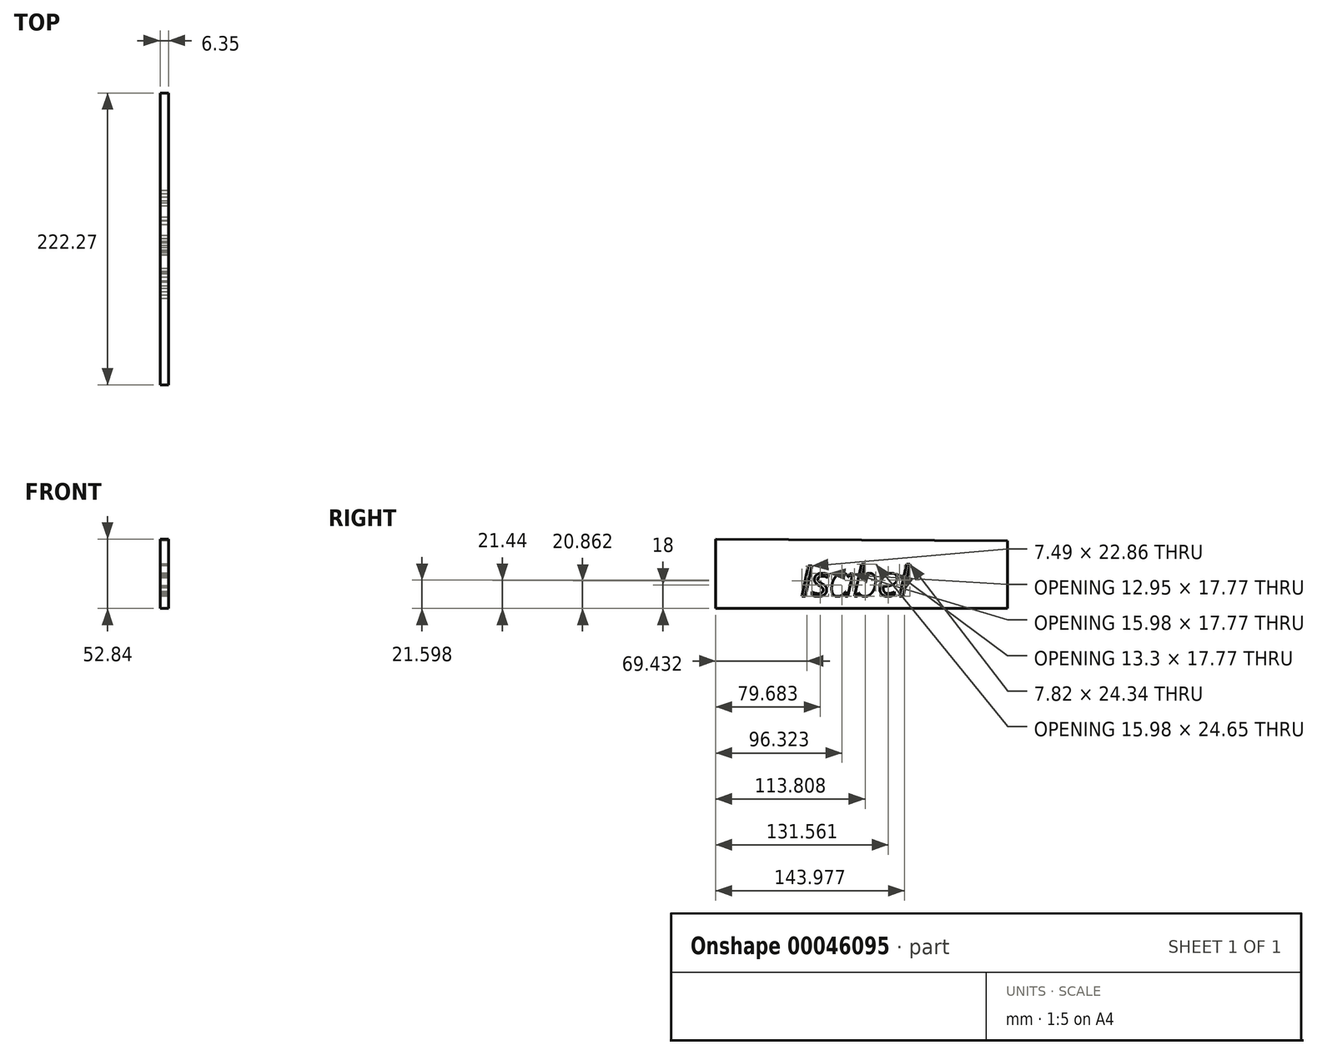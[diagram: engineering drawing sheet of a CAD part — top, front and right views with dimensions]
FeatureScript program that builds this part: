
annotation { "Feature Type Name" : "Feature", "Feature Type Description" : "" }
export const myFeature = defineFeature(function(context is Context, id is Id, definition is map)
    precondition{}
    {
        {
            var Q0;
            Q0=qCreatedBy(makeId("Right.planeOp"),FACE);
            var sketch = newSketch(context, id + "F0", { "sketchPlane" : qUnion([Q0])});
            skLineSegment(sketch, "E0", {"start": v(-114.27, 52.84) * mm, "end": v(-114.27, 0) * mm});
            skLineSegment(sketch, "E1", {"start": v(-114.27, 0) * mm, "end": v(108, 0) * mm});
            skLineSegment(sketch, "E2", {"start": v(108, 0) * mm, "end": v(108, 51.48) * mm});
            skLineSegment(sketch, "E3", {"start": v(108, 51.48) * mm, "end": v(-114.27, 52.84) * mm});
            skText(sketch, "E4", { "text": "Isabel\n", "fontName": "OpenSans-Italic.ttf"});
            const initialGuessF0  = {"E4": [-0.04993, 0.00943, 1, 0, 0.02306]};
            skSetInitialGuess(sketch, initialGuessF0);
            skSolve(sketch);
        }
        {
            var Q0;
            Q0 = qSketchRegion(id + "F0", true);
            extrude(context, id + "F1", {"entities" : qUnion([Q0]), "depth" : 6.35 * mm});
        }
    });
